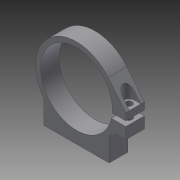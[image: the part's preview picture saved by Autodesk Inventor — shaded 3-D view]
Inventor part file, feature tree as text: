
AUTODESK INVENTOR PART (.ipt)
format: ipt  version: 2014 SP1 (Build 180222100, 222)  size: 134,656 bytes
history: native  units: in
note: dims shown in document units (in); Inventor stores cm internally (conversion verified against a paired STEP export)
features: sketch x5, other x3
ambient origin geometry x8: Origin, YZ Plane, XZ Plane, XY Plane, X Axis, Y Axis, Z Axis, Center Point
bodies: Solid1 (feature_tree)
feature tree (8):
  other  "Motor Mount.ipt"
  other  "Solid1::Motor Mount.ipt"
  other  "TaggingFeature1"
  sketch  "Sketch1"  dims[d0=0.3937in]
  sketch  "Sketch2"  dims[d1=1.65in d9=0.375in d10=0.0in d12=1.061in d13=0.138in d14=0.138in d15=0.375in d16=0.0in d21=0.125in d22=0.138in d23=1.0in d24=0.0in d26=0.4in d27=0.23in d28=0.125in d29=0.0in d30=0.375in d31=0.0in]
  sketch  "Sketch3"
  sketch  "Sketch4"
  sketch  "Sketch5"
